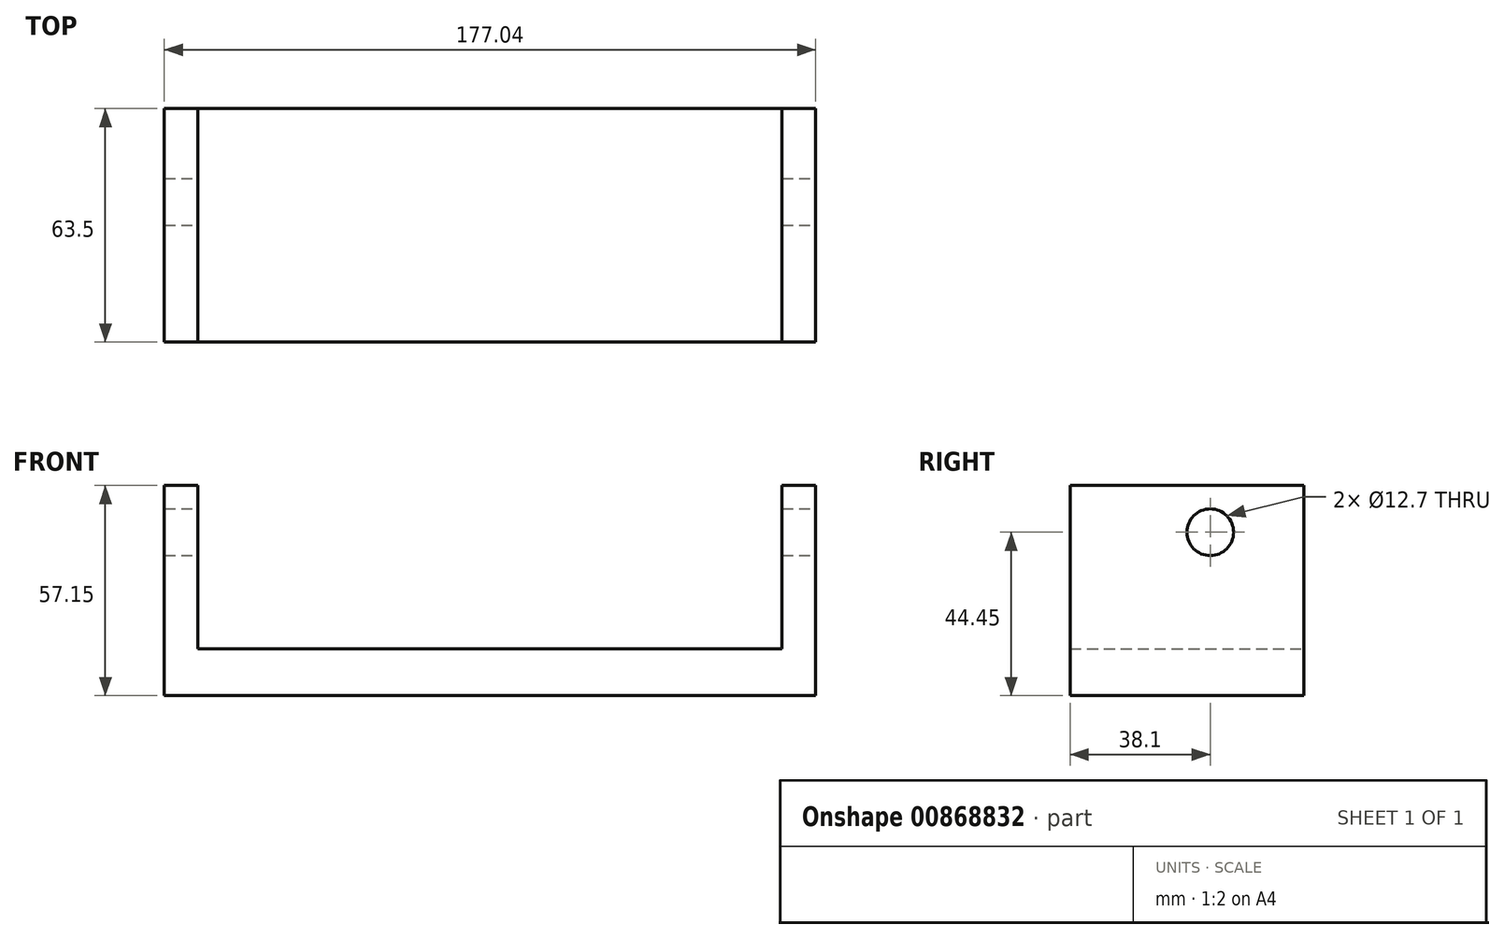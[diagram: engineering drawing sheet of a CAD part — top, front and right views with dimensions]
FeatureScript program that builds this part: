
annotation { "Feature Type Name" : "Feature", "Feature Type Description" : "" }
export const myFeature = defineFeature(function(context is Context, id is Id, definition is map)
    precondition{}
    {
        {
            var Q0;
            Q0=qCreatedBy(makeId("Front.planeOp"),FACE);
            var sketch = newSketch(context, id + "F0", { "sketchPlane" : qUnion([Q0])});
            skLineSegment(sketch, "E0.bottom", {"start": v(0, 57.15) * mm, "end": v(9.14, 57.15) * mm});
            skLineSegment(sketch, "E0.top", {"start": v(0, 0) * mm, "end": v(177.04, 0) * mm});
            skLineSegment(sketch, "E0.left", {"start": v(0, 57.15) * mm, "end": v(0, 0) * mm});
            skLineSegment(sketch, "E0.right", {"start": v(177.04, 57.15) * mm, "end": v(177.04, 0) * mm});
            skLineSegment(sketch, "E1", {"start": v(9.14, 57.15) * mm, "end": v(9.14, 12.7) * mm});
            skLineSegment(sketch, "E2", {"start": v(9.14, 12.7) * mm, "end": v(167.9, 12.7) * mm});
            skLineSegment(sketch, "E3", {"start": v(167.9, 12.7) * mm, "end": v(167.9, 57.15) * mm});
            skLineSegment(sketch, "E4.trimOffspring", {"start": v(167.9, 57.15) * mm, "end": v(177.04, 57.15) * mm});
            skSolve(sketch);
        }
        {
            var Q0;
            Q0=makeQuery(id+"F0.imprint","IMPRINT",FACE,{"disambiguationData":[TD([[makeQuery(id+"F0.imprint","IMPRINT",EDGE,{"derivedFrom":sQuery(id+"F0.wireOp",EDGE,"E0.bottom")}),-1.0]])]});
            extrude(context, id + "F1", {"entities" : qUnion([Q0]), "depth" : 63.5 * mm, "offsetDistance" : 25.4 * mm});
        }
        {
            var Q0;
            Q0=makeQuery(id+"F1.opExtrude","SWEPT_FACE",FACE,{"disambiguationData":[OSD([sQuery(id+"F0.wireOp",EDGE,"E0.right")])]});
            var sketch = newSketch(context, id + "F2", { "sketchPlane" : qUnion([Q0])});
            skCircle(sketch, "E5", {"center": v(-25.4, 44.45) * mm, "radius": 6.35 * mm});
            skSolve(sketch);
        }
        {
            var Q0;
            Q0=makeQuery(id+"F2.imprint","IMPRINT",FACE,{"disambiguationData":[TD([[makeQuery(id+"F2.imprint","IMPRINT",EDGE,{"derivedFrom":sQuery(id+"F2.wireOp",EDGE,"E5")}),1.0]])]});
            extrude(context, id + "F3", {"entities" : qUnion([Q0]), "operationType" : NewBodyOperationType.REMOVE, "endBound" : BoundingType.THROUGH_ALL, "oppositeDirection" : true, "depth" : 25.4 * mm, "offsetDistance" : 25.4 * mm});
        }
    });
